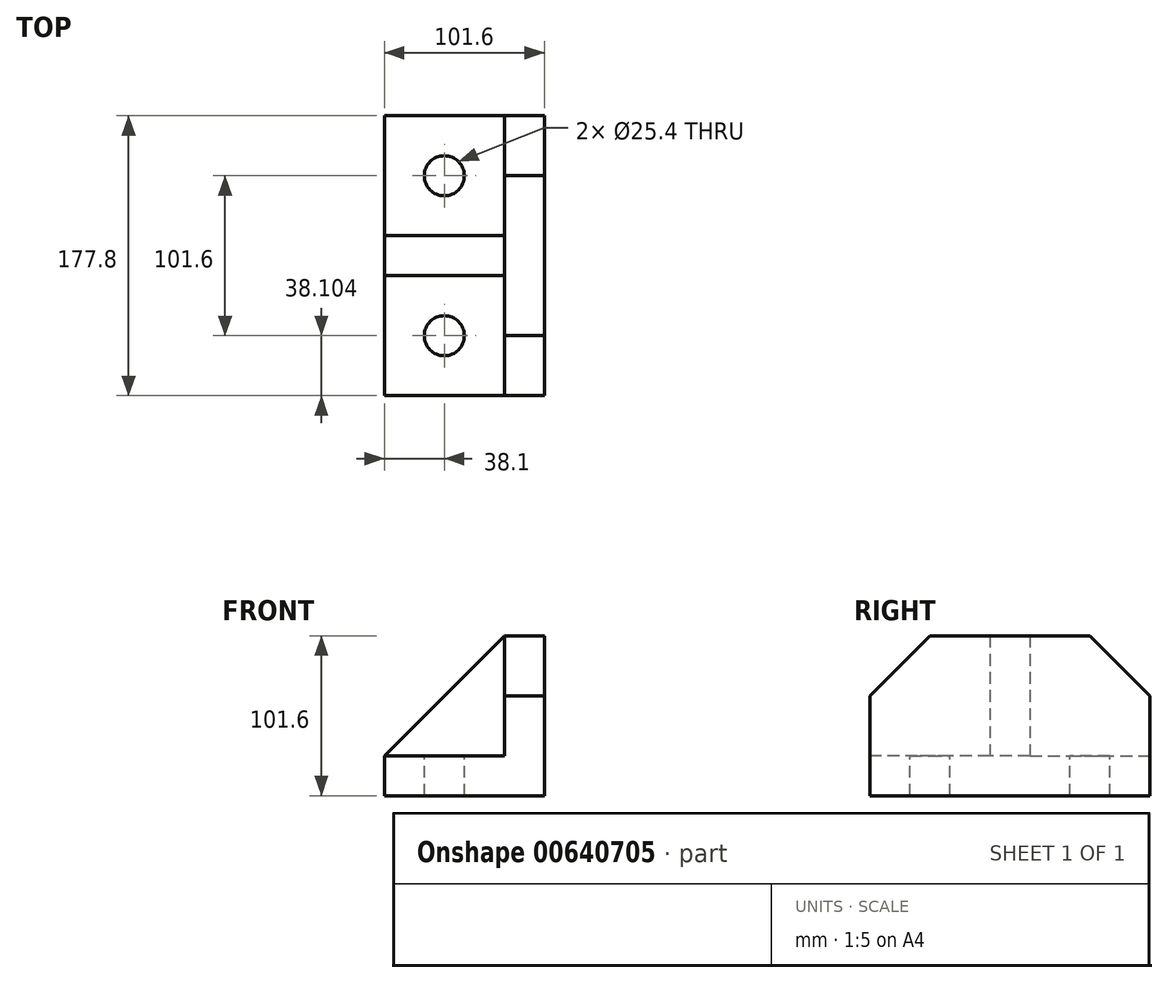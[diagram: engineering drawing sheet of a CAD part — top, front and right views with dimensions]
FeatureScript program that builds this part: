
annotation { "Feature Type Name" : "Feature", "Feature Type Description" : "" }
export const myFeature = defineFeature(function(context is Context, id is Id, definition is map)
    precondition{}
    {
        {
            var Q0;
            Q0=qCreatedBy(makeId("Top.planeOp"),FACE);
            var sketch = newSketch(context, id + "F0", { "sketchPlane" : qUnion([Q0])});
            skLineSegment(sketch, "E0.bottom", {"start": v(-33.23, 61.85) * mm, "end": v(68.37, 61.85) * mm});
            skLineSegment(sketch, "E0.top", {"start": v(-33.23, -115.95) * mm, "end": v(68.37, -115.95) * mm});
            skLineSegment(sketch, "E0.left", {"start": v(-33.23, 61.85) * mm, "end": v(-33.23, -115.95) * mm});
            skLineSegment(sketch, "E0.right", {"start": v(68.37, 61.85) * mm, "end": v(68.37, -115.95) * mm});
            skLineSegment(sketch, "E1", {"start": v(-33.23, -115.95) * mm, "end": v(-33.23, -39.75) * mm, "construction": true});
            skLineSegment(sketch, "E2", {"start": v(-33.23, 61.85) * mm, "end": v(-33.23, -14.35) * mm, "construction": true});
            skLineSegment(sketch, "E3", {"start": v(-33.23, -39.75) * mm, "end": v(42.97, -39.75) * mm});
            skLineSegment(sketch, "E4", {"start": v(-33.23, -14.35) * mm, "end": v(42.97, -14.35) * mm});
            skLineSegment(sketch, "E5", {"start": v(42.97, -39.75) * mm, "end": v(42.97, -115.95) * mm});
            skLineSegment(sketch, "E6", {"start": v(42.97, -14.35) * mm, "end": v(42.97, 61.85) * mm});
            skLineSegment(sketch, "E7", {"start": v(42.97, -14.35) * mm, "end": v(42.97, -39.75) * mm});
            skSolve(sketch);
        }
        {
            var Q0;
            {var subQ1=sQuery(id+"F0.wireOp",EDGE,"E0.right");Q0=makeQuery(id+"F0.imprint","IMPRINT",FACE,{"disambiguationData":[TD([[makeQuery(id+"F0.imprint","IMPRINT",EDGE,{"derivedFrom":subQ1}),-1.0]])]});}
            var Q1;
            {var subQ0=sQuery(id+"F0.wireOp",EDGE,"E3");Q1=makeQuery(id+"F0.imprint","IMPRINT",FACE,{"disambiguationData":[TD([[makeQuery(id+"F0.imprint","IMPRINT",EDGE,{"derivedFrom":subQ0}),1.0]])]});}
            extrude(context, id + "F1", {"entities" : qUnion([Q0, Q1]), "depth" : 101.6 * mm, "offsetDistance" : 25.4 * mm});
        }
        {
            var Q0;
            {var subQ4=sQuery(id+"F0.wireOp",EDGE,"E4");Q0=makeQuery(id+"F0.imprint","IMPRINT",FACE,{"disambiguationData":[TD([[makeQuery(id+"F0.imprint","IMPRINT",EDGE,{"derivedFrom":subQ4}),1.0]])]});}
            var Q1;
            {var subQ4=sQuery(id+"F0.wireOp",EDGE,"E3");Q1=makeQuery(id+"F0.imprint","IMPRINT",FACE,{"disambiguationData":[TD([[makeQuery(id+"F0.imprint","IMPRINT",EDGE,{"derivedFrom":subQ4}),-1.0]])]});}
            extrude(context, id + "F2", {"entities" : qUnion([Q0, Q1]), "operationType" : NewBodyOperationType.ADD, "depth" : 25.4 * mm, "offsetDistance" : 25.4 * mm});
        }
        {
            var Q0;
            Q0=makeQuery(id+"F1.opExtrude","SWEPT_FACE",FACE,{"disambiguationData":[OSD([sQuery(id+"F0.wireOp",EDGE,"E3")])]});
            var sketch = newSketch(context, id + "F3", { "sketchPlane" : qUnion([Q0])});
            skLineSegment(sketch, "E8", {"start": v(-33.23, 25.4) * mm, "end": v(42.97, 101.6) * mm});
            skSolve(sketch);
        }
        {
            var Q0;
            Q0=makeQuery(id+"F3.imprint","IMPRINT",FACE,{"disambiguationData":[TD([[makeQuery(id+"F3.imprint","IMPRINT",EDGE,{"derivedFrom":sQuery(id+"F3.wireOp",EDGE,"E8")}),1.0]])]});
            extrude(context, id + "F4", {"entities" : qUnion([Q0]), "operationType" : NewBodyOperationType.REMOVE, "endBound" : BoundingType.THROUGH_ALL, "oppositeDirection" : true, "depth" : 25.4 * mm, "offsetDistance" : 25.4 * mm});
        }
        {
            var Q0;
            Q0=makeQuery(id+"F1.opExtrude","SWEPT_FACE",FACE,{"disambiguationData":[OSD([sQuery(id+"F0.wireOp",EDGE,"E5")])]});
            var sketch = newSketch(context, id + "F5", { "sketchPlane" : qUnion([Q0])});
            skLineSegment(sketch, "E9", {"start": v(77.85, 101.6) * mm, "end": v(77.85, 63.5) * mm, "construction": true});
            skLineSegment(sketch, "E10", {"start": v(77.85, 63.5) * mm, "end": v(115.95, 63.5) * mm, "construction": true});
            skLineSegment(sketch, "E11", {"start": v(77.85, 101.6) * mm, "end": v(115.95, 63.5) * mm});
            skSolve(sketch);
        }
        {
            var Q0;
            Q0=makeQuery(id+"F1.opExtrude","SWEPT_FACE",FACE,{"disambiguationData":[OSD([sQuery(id+"F0.wireOp",EDGE,"E6")])]});
            var sketch = newSketch(context, id + "F6", { "sketchPlane" : qUnion([Q0])});
            skLineSegment(sketch, "E12", {"start": v(-23.75, 101.6) * mm, "end": v(-23.75, 63.5) * mm, "construction": true});
            skLineSegment(sketch, "E13", {"start": v(-23.75, 63.5) * mm, "end": v(-61.85, 63.5) * mm, "construction": true});
            skLineSegment(sketch, "E14", {"start": v(-23.75, 101.6) * mm, "end": v(-61.85, 63.5) * mm});
            skSolve(sketch);
        }
        {
            var Q0;
            {var subQ0=sQuery(id+"F6.wireOp",EDGE,"E14");Q0=makeQuery(id+"F6.imprint","IMPRINT",FACE,{"disambiguationData":[TD([[makeQuery(id+"F6.imprint","IMPRINT",EDGE,{"derivedFrom":subQ0}),-1.0]])]});}
            var Q1;
            {var subQ0=sQuery(id+"F5.wireOp",EDGE,"E11");Q1=makeQuery(id+"F5.imprint","IMPRINT",FACE,{"disambiguationData":[TD([[makeQuery(id+"F5.imprint","IMPRINT",EDGE,{"derivedFrom":subQ0}),1.0]])]});}
            extrude(context, id + "F7", {"entities" : qUnion([Q0, Q1]), "operationType" : NewBodyOperationType.REMOVE, "endBound" : BoundingType.THROUGH_ALL, "oppositeDirection" : true, "depth" : 25.4 * mm, "offsetDistance" : 25.4 * mm});
        }
        {
            var Q0;
            Q0=makeQuery(id+"F2.opExtrude","CAP_FACE",FACE,{"disambiguationData":[OSD([sQuery(id+"F0.wireOp",EDGE,"E0.top"),sQuery(id+"F0.wireOp",EDGE,"E0.left"),sQuery(id+"F0.wireOp",EDGE,"E3"),sQuery(id+"F0.wireOp",EDGE,"E5")])],"isStart":false});
            var sketch = newSketch(context, id + "F8", { "sketchPlane" : qUnion([Q0])});
            skLineSegment(sketch, "E15", {"start": v(-33.23, -77.85) * mm, "end": v(4.87, -77.85) * mm, "construction": true});
            skCircle(sketch, "E16", {"center": v(4.87, -77.85) * mm, "radius": 12.7 * mm});
            skSolve(sketch);
        }
        {
            var Q0;
            Q0=makeQuery(id+"F2.opExtrude","CAP_FACE",FACE,{"disambiguationData":[OSD([sQuery(id+"F0.wireOp",EDGE,"E0.bottom"),sQuery(id+"F0.wireOp",EDGE,"E0.left"),sQuery(id+"F0.wireOp",EDGE,"E4"),sQuery(id+"F0.wireOp",EDGE,"E6")])],"isStart":false});
            var sketch = newSketch(context, id + "F9", { "sketchPlane" : qUnion([Q0])});
            skLineSegment(sketch, "E17", {"start": v(-33.23, 23.75) * mm, "end": v(4.87, 23.75) * mm, "construction": true});
            skPoint(sketch, "E17.endSnap0", {"position": v(4.87, 61.85) * mm});
            skCircle(sketch, "E18", {"center": v(4.87, 23.75) * mm, "radius": 12.7 * mm});
            skSolve(sketch);
        }
        {
            var Q0;
            Q0=makeQuery(id+"F9.imprint","IMPRINT",FACE,{"disambiguationData":[TD([[makeQuery(id+"F9.imprint","IMPRINT",EDGE,{"derivedFrom":sQuery(id+"F9.wireOp",EDGE,"E18")}),1.0]])]});
            var Q1;
            Q1=makeQuery(id+"F8.imprint","IMPRINT",FACE,{"disambiguationData":[TD([[makeQuery(id+"F8.imprint","IMPRINT",EDGE,{"derivedFrom":sQuery(id+"F8.wireOp",EDGE,"E16")}),1.0]])]});
            extrude(context, id + "F10", {"entities" : qUnion([Q0, Q1]), "operationType" : NewBodyOperationType.REMOVE, "endBound" : BoundingType.THROUGH_ALL, "oppositeDirection" : true, "depth" : 25.4 * mm, "offsetDistance" : 25.4 * mm});
        }
    });
